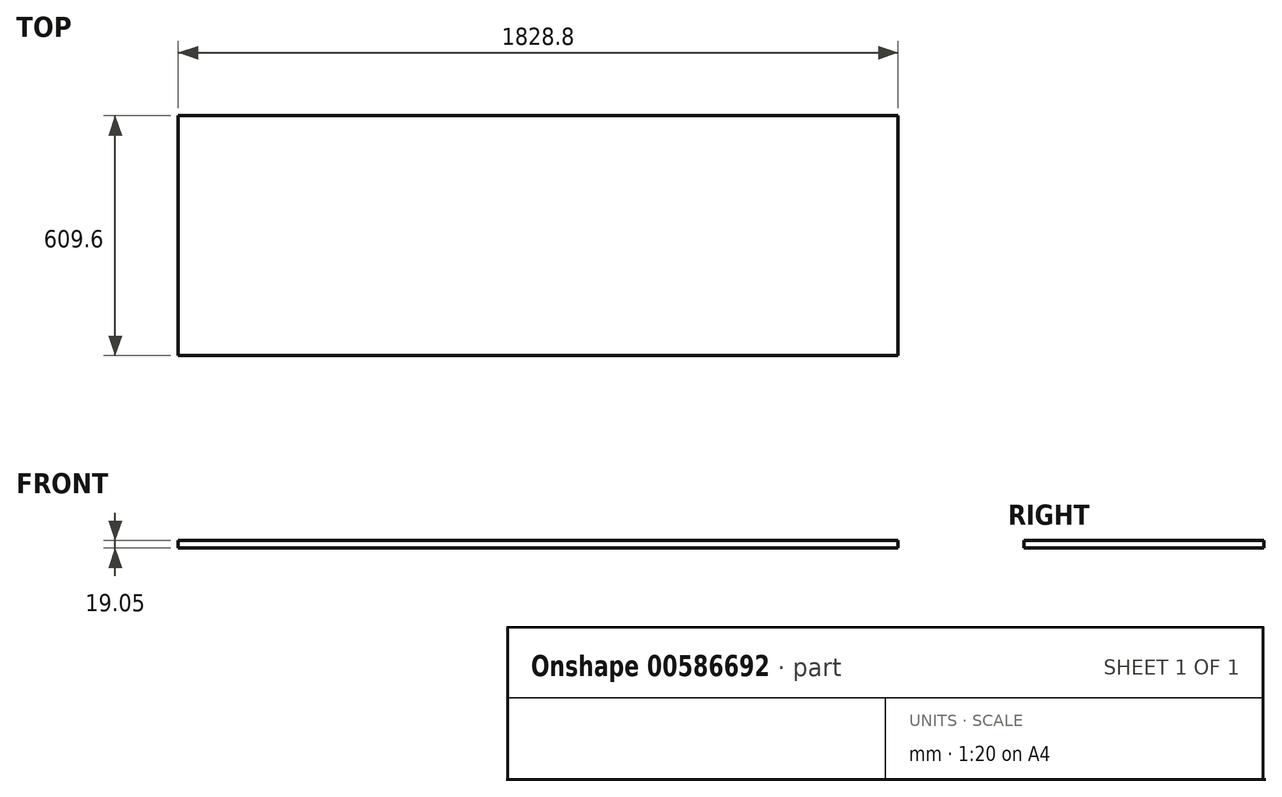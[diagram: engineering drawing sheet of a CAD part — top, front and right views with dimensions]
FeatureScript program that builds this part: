
annotation { "Feature Type Name" : "Feature", "Feature Type Description" : "" }
export const myFeature = defineFeature(function(context is Context, id is Id, definition is map)
    precondition{}
    {
        {
            var Q0;
            Q0=qCreatedBy(makeId("Top.planeOp"),FACE);
            var sketch = newSketch(context, id + "F0", { "sketchPlane" : qUnion([Q0])});
            skLineSegment(sketch, "E0.bottom", {"start": v(-769.18, -305.59) * mm, "end": v(1059.62, -305.59) * mm});
            skLineSegment(sketch, "E0.top", {"start": v(-769.18, 304.01) * mm, "end": v(1059.62, 304.01) * mm});
            skLineSegment(sketch, "E0.left", {"start": v(-769.18, -305.59) * mm, "end": v(-769.18, 304.01) * mm});
            skLineSegment(sketch, "E0.right", {"start": v(1059.62, -305.59) * mm, "end": v(1059.62, 304.01) * mm});
            skSolve(sketch);
        }
        {
            var Q0;
            Q0 = qSketchRegion(id + "F0", true);
            extrude(context, id + "F1", {"entities" : qUnion([Q0]), "depth" : 19.05 * mm, "offsetDistance" : 25.4 * mm});
        }
    });
